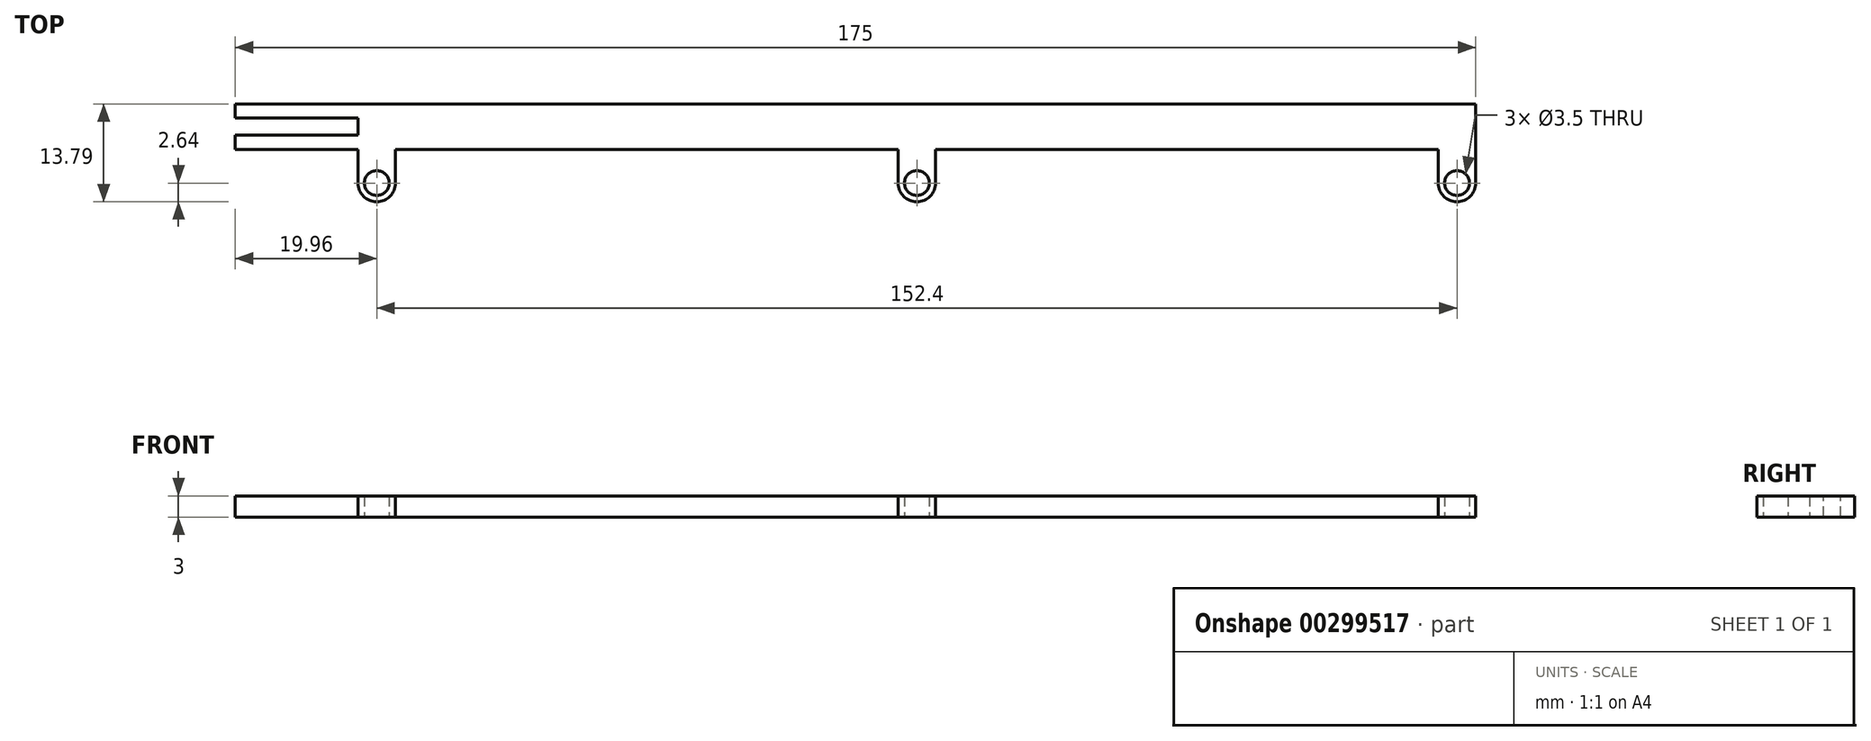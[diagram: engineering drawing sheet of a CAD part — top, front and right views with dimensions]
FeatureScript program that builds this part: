
annotation { "Feature Type Name" : "Feature", "Feature Type Description" : "" }
export const myFeature = defineFeature(function(context is Context, id is Id, definition is map)
    precondition{}
    {
        {
            var Q0;
            Q0=qCreatedBy(makeId("Top.planeOp"),FACE);
            var sketch = newSketch(context, id + "F0", { "sketchPlane" : qUnion([Q0])});
            skLineSegment(sketch, "E0.bottom", {"start": v(129.86, 3.2) * mm, "end": v(-129.86, 3.2) * mm});
            skLineSegment(sketch, "E0.top", {"start": v(129.86, -3.2) * mm, "end": v(-129.86, -3.2) * mm});
            skLineSegment(sketch, "E0.left", {"start": v(129.86, 3.2) * mm, "end": v(129.86, -3.2) * mm});
            skLineSegment(sketch, "E0.right", {"start": v(-129.86, 3.2) * mm, "end": v(-129.86, -3.2) * mm});
            skPoint(sketch, "E0.middle", {"position": v(0, 0) * mm});
            skSolve(sketch);
        }
        {
            var Q0;
            Q0=makeQuery(id+"F0.imprint","IMPRINT",FACE,{"disambiguationData":[TD([[makeQuery(id+"F0.imprint","IMPRINT",EDGE,{"derivedFrom":sQuery(id+"F0.wireOp",EDGE,"E0.bottom")}),1.0]])]});
            extrude(context, id + "F1", {"entities" : qUnion([Q0]), "depth" : 3 * mm});
        }
        {
            var Q0;
            Q0=qCreatedBy(makeId("Top.planeOp"),FACE);
            var sketch = newSketch(context, id + "F2", { "sketchPlane" : qUnion([Q0])});
            skLineSegment(sketch, "E1.bottom", {"start": v(129.86, -3.2) * mm, "end": v(124.58, -3.2) * mm});
            skLineSegment(sketch, "E1.top", {"start": v(129.86, -10.59) * mm, "end": v(124.58, -10.59) * mm});
            skLineSegment(sketch, "E1.left", {"start": v(129.86, -3.2) * mm, "end": v(129.86, -10.59) * mm});
            skLineSegment(sketch, "E1.right", {"start": v(124.58, -3.2) * mm, "end": v(124.58, -10.59) * mm});
            skCircle(sketch, "E2", {"center": v(127.22, -7.95) * mm, "radius": 1.75 * mm});
            skLineSegment(sketch, "E3", {"start": v(127.22, -7.95) * mm, "end": v(127.22, -10.59) * mm});
            skLineSegment(sketch, "E4", {"start": v(127.22, -7.95) * mm, "end": v(124.58, -7.95) * mm});
            skLineSegment(sketch, "E5.bottom", {"start": v(53.66, -3.2) * mm, "end": v(48.38, -3.2) * mm});
            skLineSegment(sketch, "E5.top", {"start": v(53.66, -10.59) * mm, "end": v(48.38, -10.59) * mm});
            skLineSegment(sketch, "E5.left", {"start": v(53.66, -3.2) * mm, "end": v(53.66, -10.59) * mm});
            skLineSegment(sketch, "E5.right", {"start": v(48.38, -3.2) * mm, "end": v(48.38, -10.6) * mm});
            skCircle(sketch, "E6", {"center": v(51.02, -7.95) * mm, "radius": 1.75 * mm});
            skPoint(sketch, "E6.centerSnap0", {"position": v(51.02, -10.6) * mm});
            skLineSegment(sketch, "E7", {"start": v(51.02, -7.95) * mm, "end": v(48.38, -7.95) * mm});
            skPoint(sketch, "E7.endSnap0", {"position": v(48.38, -6.9) * mm});
            skLineSegment(sketch, "E8.bottom", {"start": v(-27.82, -3.2) * mm, "end": v(-22.54, -3.2) * mm});
            skLineSegment(sketch, "E8.top", {"start": v(-27.82, -10.6) * mm, "end": v(-22.54, -10.6) * mm});
            skLineSegment(sketch, "E8.left", {"start": v(-27.82, -3.2) * mm, "end": v(-27.82, -10.6) * mm});
            skLineSegment(sketch, "E8.right", {"start": v(-22.54, -3.2) * mm, "end": v(-22.54, -10.6) * mm});
            skCircle(sketch, "E9", {"center": v(-25.18, -7.95) * mm, "radius": 1.75 * mm});
            skLineSegment(sketch, "E10", {"start": v(-25.18, -7.95) * mm, "end": v(-27.82, -7.95) * mm});
            skSolve(sketch);
        }
        {
            var Q0;
            {var subQ1=sQuery(id+"F2.wireOp",EDGE,"E1.bottom");Q0=makeQuery(id+"F2.imprint","IMPRINT",FACE,{"disambiguationData":[TD([[makeQuery(id+"F2.imprint","IMPRINT",EDGE,{"derivedFrom":subQ1}),1.0]])]});}
            var Q1;
            {var subQ1=sQuery(id+"F2.wireOp",EDGE,"E1.top");var subQ7=sQuery(id+"F2.wireOp",EDGE,"E1.right");var subQ8=makeQuery(id+"F2.imprint","INTERSECT",VERTEX,{"derivedFrom":[subQ1,subQ7]});Q1=makeQuery(id+"F2.imprint","IMPRINT",FACE,{"disambiguationData":[TD([[makeQuery(id+"F2.imprint","IMPRINT",EDGE,{"disambiguationData":[TD([[subQ8,1.0]])],"derivedFrom":subQ1}),-1.0]])]});}
            var Q2;
            {var subQ1=sQuery(id+"F2.wireOp",EDGE,"E5.bottom");Q2=makeQuery(id+"F2.imprint","IMPRINT",FACE,{"disambiguationData":[TD([[makeQuery(id+"F2.imprint","IMPRINT",EDGE,{"derivedFrom":subQ1}),1.0]])]});}
            var Q3;
            {var subQ3=sQuery(id+"F2.wireOp",EDGE,"E8.bottom");Q3=makeQuery(id+"F2.imprint","IMPRINT",FACE,{"disambiguationData":[TD([[makeQuery(id+"F2.imprint","IMPRINT",EDGE,{"derivedFrom":subQ3}),-1.0]])]});}
            extrude(context, id + "F3", {"entities" : qUnion([Q0, Q1, Q2, Q3]), "operationType" : NewBodyOperationType.ADD, "depth" : 3 * mm});
        }
        {
            var Q0;
            Q0=makeQuery(id+"F3.opExtrude","SWEPT_EDGE",EDGE,{"disambiguationData":[OSD([sQuery(id+"F2.wireOp",EDGE,"E5.top"),sQuery(id+"F2.wireOp",EDGE,"E5.right")])]});
            var Q1;
            Q1=makeQuery(id+"F3.opExtrude","SWEPT_EDGE",EDGE,{"disambiguationData":[OSD([sQuery(id+"F2.wireOp",EDGE,"E5.top"),sQuery(id+"F2.wireOp",EDGE,"E5.left")])]});
            var Q2;
            Q2=makeQuery(id+"F3.opExtrude","SWEPT_EDGE",EDGE,{"disambiguationData":[OSD([sQuery(id+"F2.wireOp",EDGE,"E1.top"),sQuery(id+"F2.wireOp",EDGE,"E1.right")])]});
            var Q3;
            Q3=makeQuery(id+"F3.opExtrude","SWEPT_EDGE",EDGE,{"disambiguationData":[OSD([sQuery(id+"F2.wireOp",EDGE,"E1.top"),sQuery(id+"F2.wireOp",EDGE,"E1.left")])]});
            var Q4;
            Q4=makeQuery(id+"F3.opExtrude","SWEPT_EDGE",EDGE,{"disambiguationData":[OSD([sQuery(id+"F2.wireOp",EDGE,"E8.top"),sQuery(id+"F2.wireOp",EDGE,"E8.left")])]});
            var Q5;
            Q5=makeQuery(id+"F3.opExtrude","SWEPT_EDGE",EDGE,{"disambiguationData":[OSD([sQuery(id+"F2.wireOp",EDGE,"E8.top"),sQuery(id+"F2.wireOp",EDGE,"E8.right")])]});
            fillet(context, id + "F4", {"entities" : qUnion([Q0, Q1, Q2, Q3, Q4, Q5]), "radius" : 2.64 * mm, "tangentPropagation" : true, "allowEdgeOverflow" : false});
        }
        {
            var Q0;
            Q0=makeQuery(id+"F3.boolean.opBoolean","MERGE",FACE,{"derivedFrom":[makeQuery(id+"F1.opExtrude","CAP_FACE",FACE,{"disambiguationData":[OSD([sQuery(id+"F0.wireOp",EDGE,"E0.bottom"),sQuery(id+"F0.wireOp",EDGE,"E0.top"),sQuery(id+"F0.wireOp",EDGE,"E0.left"),sQuery(id+"F0.wireOp",EDGE,"E0.right")])],"isStart":false}),makeQuery(id+"F3.opExtrude","CAP_FACE",FACE,{"disambiguationData":[OSD([sQuery(id+"F2.wireOp",EDGE,"E1.bottom"),sQuery(id+"F2.wireOp",EDGE,"E1.top"),sQuery(id+"F2.wireOp",EDGE,"E1.left"),sQuery(id+"F2.wireOp",EDGE,"E1.right"),sQuery(id+"F2.wireOp",EDGE,"E2")])],"isStart":false}),makeQuery(id+"F3.opExtrude","CAP_FACE",FACE,{"disambiguationData":[OSD([sQuery(id+"F2.wireOp",EDGE,"E5.bottom"),sQuery(id+"F2.wireOp",EDGE,"E5.top"),sQuery(id+"F2.wireOp",EDGE,"E5.left"),sQuery(id+"F2.wireOp",EDGE,"E5.right"),sQuery(id+"F2.wireOp",EDGE,"E6")])],"isStart":false}),makeQuery(id+"F3.opExtrude","CAP_FACE",FACE,{"disambiguationData":[OSD([sQuery(id+"F2.wireOp",EDGE,"E8.bottom"),sQuery(id+"F2.wireOp",EDGE,"E8.top"),sQuery(id+"F2.wireOp",EDGE,"E8.left"),sQuery(id+"F2.wireOp",EDGE,"E8.right"),sQuery(id+"F2.wireOp",EDGE,"E9")])],"isStart":false})]});
            var sketch = newSketch(context, id + "F5", { "sketchPlane" : qUnion([Q0])});
            skLineSegment(sketch, "E11.bottom", {"start": v(-129.86, 3.2) * mm, "end": v(-45.14, 3.2) * mm});
            skLineSegment(sketch, "E11.top", {"start": v(-129.86, -3.2) * mm, "end": v(-45.14, -3.2) * mm});
            skLineSegment(sketch, "E11.left", {"start": v(-129.86, 3.2) * mm, "end": v(-129.86, -3.2) * mm});
            skLineSegment(sketch, "E11.right", {"start": v(-45.14, 3.2) * mm, "end": v(-45.14, -3.2) * mm});
            skLineSegment(sketch, "E12.bottom", {"start": v(-45.14, 1.2) * mm, "end": v(-27.82, 1.2) * mm});
            skLineSegment(sketch, "E12.top", {"start": v(-45.14, -1.2) * mm, "end": v(-27.82, -1.2) * mm});
            skLineSegment(sketch, "E12.left", {"start": v(-45.14, 1.2) * mm, "end": v(-45.14, -1.2) * mm});
            skLineSegment(sketch, "E12.right", {"start": v(-27.82, 1.2) * mm, "end": v(-27.82, -1.2) * mm});
            skSolve(sketch);
        }
        {
            var Q0;
            {var subQ1=sQuery(id+"F5.wireOp",EDGE,"E11.bottom");Q0=makeQuery(id+"F5.imprint","IMPRINT",FACE,{"disambiguationData":[TD([[makeQuery(id+"F5.imprint","IMPRINT",EDGE,{"derivedFrom":subQ1}),1.0]])]});}
            var Q1;
            Q1=makeQuery(id+"F5.imprint","IMPRINT",FACE,{"disambiguationData":[TD([[makeQuery(id+"F5.imprint","IMPRINT",EDGE,{"derivedFrom":sQuery(id+"F5.wireOp",EDGE,"E12.bottom")}),-1.0]])]});
            extrude(context, id + "F6", {"entities" : qUnion([Q0, Q1]), "operationType" : NewBodyOperationType.REMOVE, "endBound" : BoundingType.THROUGH_ALL, "oppositeDirection" : true, "depth" : 25 * mm});
        }
    });
